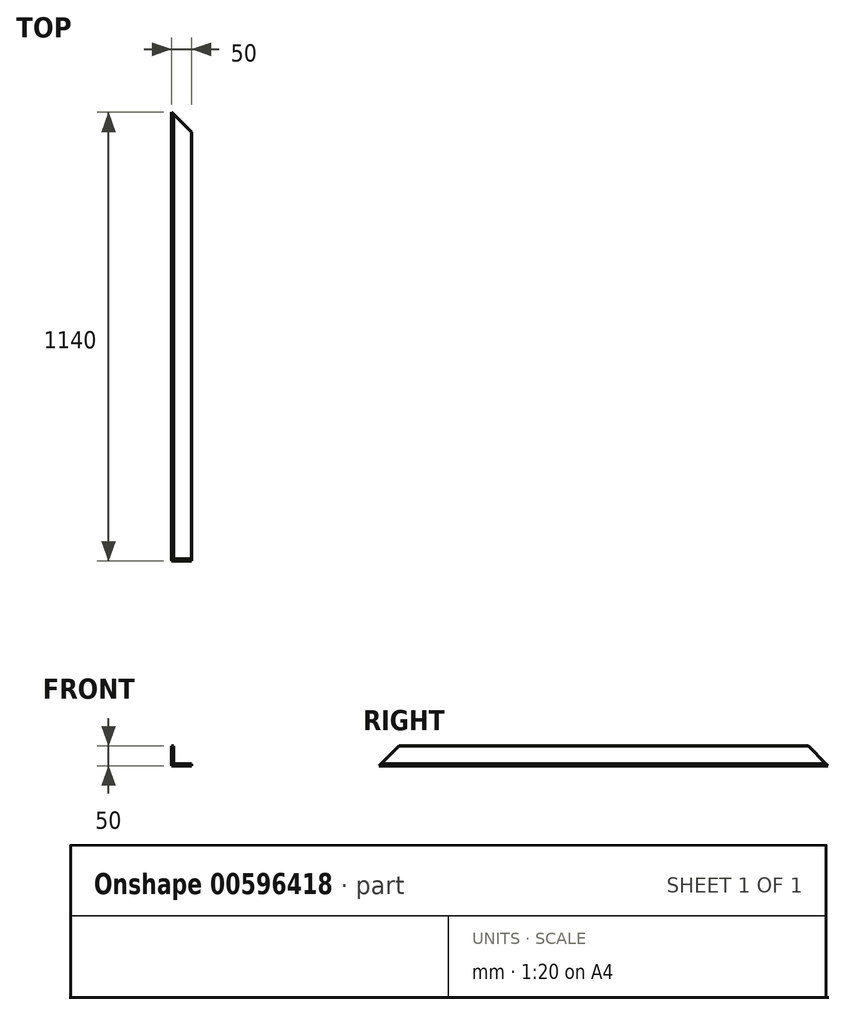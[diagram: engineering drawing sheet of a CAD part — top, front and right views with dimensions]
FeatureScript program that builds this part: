
annotation { "Feature Type Name" : "Feature", "Feature Type Description" : "" }
export const myFeature = defineFeature(function(context is Context, id is Id, definition is map)
    precondition{}
    {
        {
            var Q0;
            Q0=qCreatedBy(makeId("Front.planeOp"),FACE);
            var sketch = newSketch(context, id + "F0", { "sketchPlane" : qUnion([Q0])});
            skLineSegment(sketch, "E0", {"start": v(0, 0) * mm, "end": v(50, 0) * mm});
            skLineSegment(sketch, "E1", {"start": v(0, 0) * mm, "end": v(0, 50) * mm});
            skLineSegment(sketch, "E2.0", {"start": v(5, 5) * mm, "end": v(5, 50) * mm});
            skLineSegment(sketch, "E2.1", {"start": v(5, 5) * mm, "end": v(50, 5) * mm});
            skLineSegment(sketch, "E3", {"start": v(5, 50) * mm, "end": v(0, 50) * mm});
            skLineSegment(sketch, "E4", {"start": v(50, 5) * mm, "end": v(50, 0) * mm});
            skSolve(sketch);
        }
        {
            var Q0;
            Q0=makeQuery(id+"F0.imprint","IMPRINT",FACE,{"disambiguationData":[TD([[makeQuery(id+"F0.imprint","IMPRINT",EDGE,{"derivedFrom":sQuery(id+"F0.wireOp",EDGE,"E0")}),1.0]])]});
            extrude(context, id + "F1", {"entities" : qUnion([Q0]), "endBound" : BoundingType.SYMMETRIC, "depth" : 1140 * mm, "offsetDistance" : 25 * mm});
        }
        {
            var Q0;
            Q0=makeQuery(id+"F1.opExtrude","SWEPT_FACE",FACE,{"disambiguationData":[OSD([sQuery(id+"F0.wireOp",EDGE,"E1")])]});
            var sketch = newSketch(context, id + "F2", { "sketchPlane" : qUnion([Q0])});
            skLineSegment(sketch, "E5", {"start": v(570, 0) * mm, "end": v(520, 50) * mm});
            skLineSegment(sketch, "E6", {"start": v(-570, 0) * mm, "end": v(-520, 50) * mm});
            skSolve(sketch);
        }
        {
            var Q0;
            {var subQ0=sQuery(id+"F2.wireOp",EDGE,"E6");Q0=makeQuery(id+"F2.imprint","IMPRINT",FACE,{"disambiguationData":[TD([[makeQuery(id+"F2.imprint","IMPRINT",EDGE,{"derivedFrom":subQ0}),1.0]])]});}
            var Q1;
            {var subQ0=sQuery(id+"F2.wireOp",EDGE,"E5");Q1=makeQuery(id+"F2.imprint","IMPRINT",FACE,{"disambiguationData":[TD([[makeQuery(id+"F2.imprint","IMPRINT",EDGE,{"derivedFrom":subQ0}),-1.0]])]});}
            extrude(context, id + "F3", {"entities" : qUnion([Q0, Q1]), "operationType" : NewBodyOperationType.REMOVE, "oppositeDirection" : true, "depth" : 50 * mm, "offsetDistance" : 25 * mm});
        }
        {
            var Q0;
            Q0=makeQuery(id+"F1.opExtrude","SWEPT_FACE",FACE,{"disambiguationData":[OSD([sQuery(id+"F0.wireOp",EDGE,"E0")])]});
            var sketch = newSketch(context, id + "F4", { "sketchPlane" : qUnion([Q0])});
            skLineSegment(sketch, "E7", {"start": v(0, -570) * mm, "end": v(50, -520) * mm});
            skSolve(sketch);
        }
        {
            var Q0;
            {var subQ0=sQuery(id+"F4.wireOp",EDGE,"4rBVaWI2-HdZK-pSb7-BKfN-tNmcRUyPUiNw");Q0=makeQuery(id+"F4.imprint","IMPRINT",FACE,{"disambiguationData":[TD([[makeQuery(id+"F4.imprint","IMPRINT",EDGE,{"derivedFrom":subQ0}),1.0]])]});}
            var Q1;
            {var subQ0=sQuery(id+"F4.wireOp",EDGE,"E7");Q1=makeQuery(id+"F4.imprint","IMPRINT",FACE,{"disambiguationData":[TD([[makeQuery(id+"F4.imprint","IMPRINT",EDGE,{"derivedFrom":subQ0}),-1.0]])]});}
            extrude(context, id + "F5", {"entities" : qUnion([Q0, Q1]), "operationType" : NewBodyOperationType.REMOVE, "oppositeDirection" : true, "depth" : 50 * mm, "offsetDistance" : 25 * mm});
        }
    });
